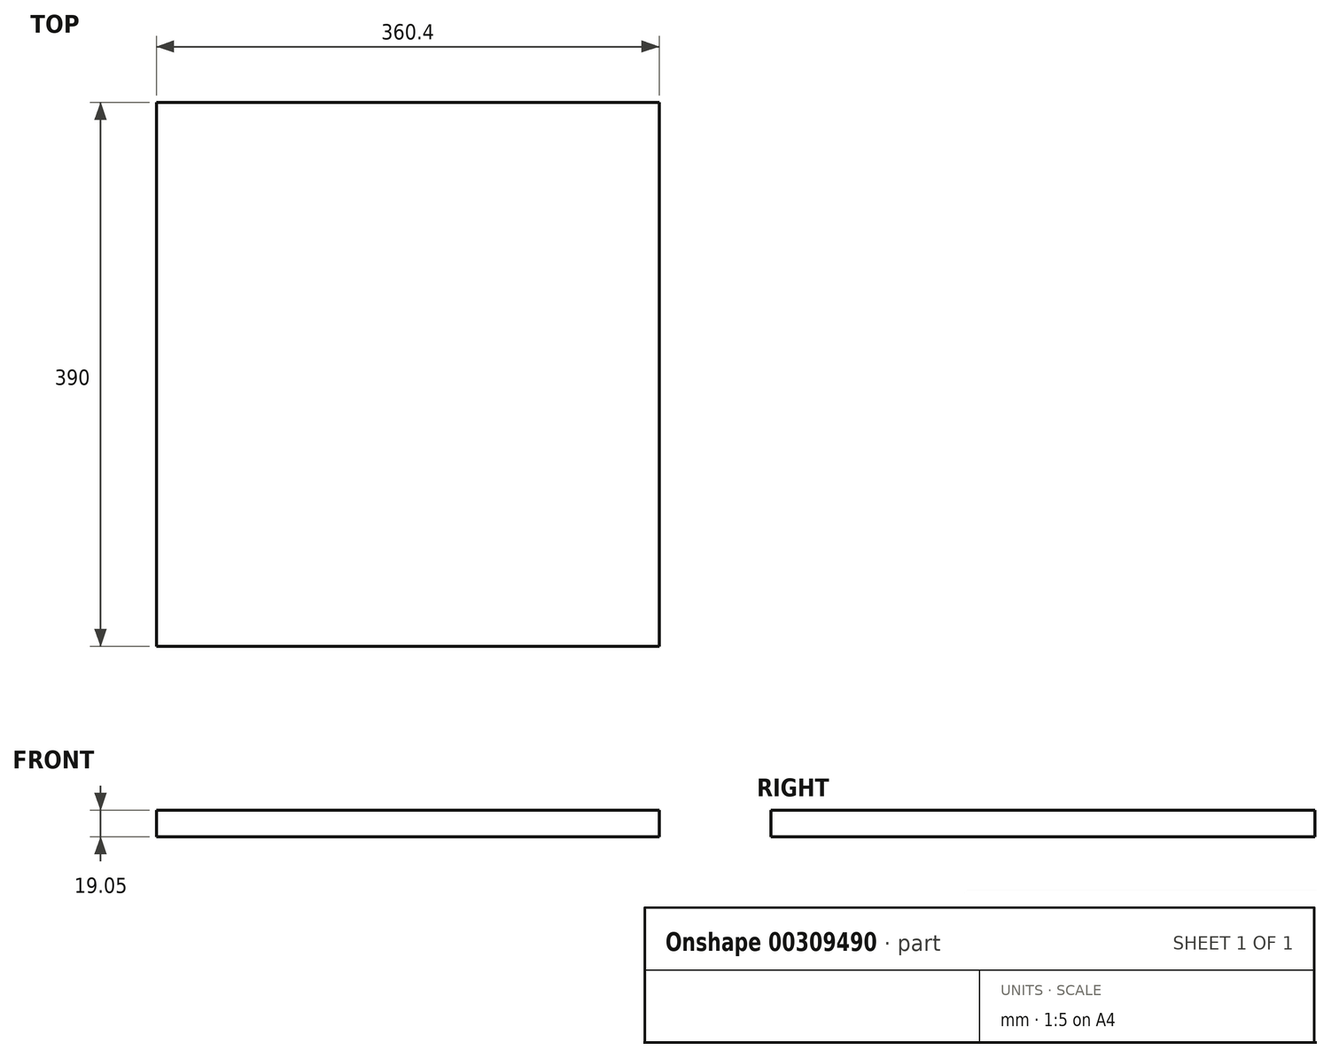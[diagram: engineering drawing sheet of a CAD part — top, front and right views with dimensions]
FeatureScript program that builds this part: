
annotation { "Feature Type Name" : "Feature", "Feature Type Description" : "" }
export const myFeature = defineFeature(function(context is Context, id is Id, definition is map)
    precondition{}
    {
        {
            var Q0;
            Q0=qCreatedBy(makeId("Top.planeOp"),FACE);
            var sketch = newSketch(context, id + "F0", { "sketchPlane" : qUnion([Q0])});
            skLineSegment(sketch, "E0.bottom", {"start": v(180.2, -195) * mm, "end": v(-180.2, -195) * mm});
            skLineSegment(sketch, "E0.top", {"start": v(180.2, 195) * mm, "end": v(-180.2, 195) * mm});
            skLineSegment(sketch, "E0.left", {"start": v(180.2, -195) * mm, "end": v(180.2, 195) * mm});
            skLineSegment(sketch, "E0.right", {"start": v(-180.2, -195) * mm, "end": v(-180.2, 195) * mm});
            skPoint(sketch, "E0.middle", {"position": v(0, 0) * mm});
            skSolve(sketch);
        }
        {
            var Q0;
            Q0=makeQuery(id+"F0.imprint","IMPRINT",FACE,{"disambiguationData":[TD([[makeQuery(id+"F0.imprint","IMPRINT",EDGE,{"derivedFrom":sQuery(id+"F0.wireOp",EDGE,"E0.bottom")}),-1.0]])]});
            extrude(context, id + "F1", {"entities" : qUnion([Q0]), "depth" : 19.05 * mm});
        }
    });
